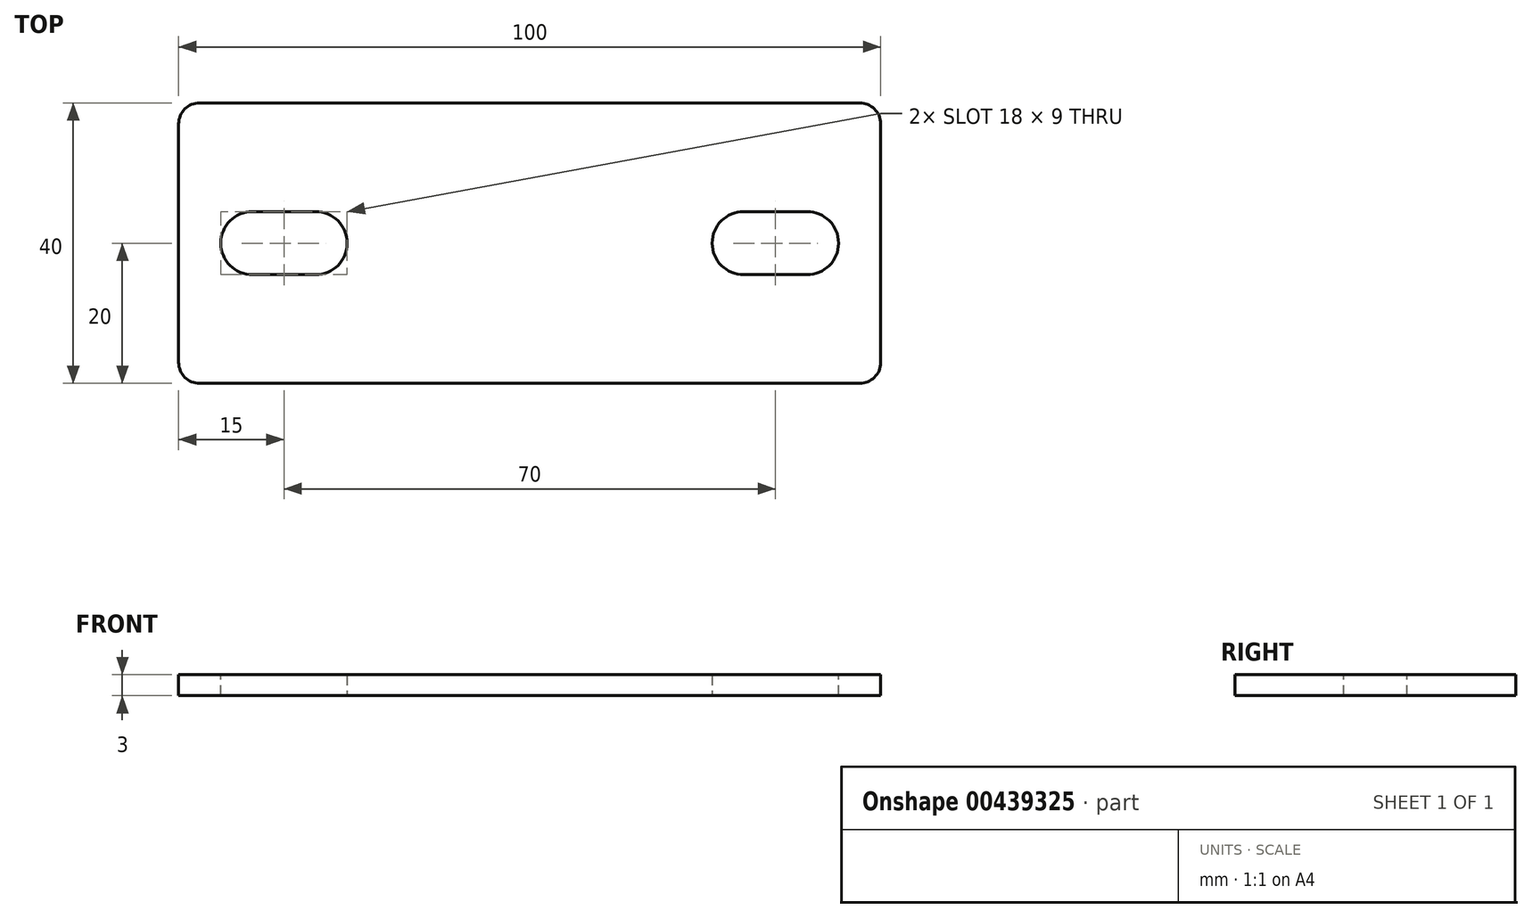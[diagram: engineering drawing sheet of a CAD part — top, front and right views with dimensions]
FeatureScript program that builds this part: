
annotation { "Feature Type Name" : "Feature", "Feature Type Description" : "" }
export const myFeature = defineFeature(function(context is Context, id is Id, definition is map)
    precondition{}
    {
        {
            var Q0;
            Q0=qCreatedBy(makeId("Top.planeOp"),FACE);
            var sketch = newSketch(context, id + "F0", { "sketchPlane" : qUnion([Q0])});
            skLineSegment(sketch, "E0.bottom", {"start": v(50, 20) * mm, "end": v(-50, 20) * mm});
            skLineSegment(sketch, "E0.top", {"start": v(50, -20) * mm, "end": v(-50, -20) * mm});
            skLineSegment(sketch, "E0.left", {"start": v(50, 20) * mm, "end": v(50, -20) * mm});
            skLineSegment(sketch, "E0.right", {"start": v(-50, 20) * mm, "end": v(-50, -20) * mm});
            skPoint(sketch, "E0.middle", {"position": v(0, 0) * mm});
            skSolve(sketch);
        }
        {
            var Q0;
            Q0=makeQuery(id+"F0.imprint","IMPRINT",FACE,{"disambiguationData":[TD([[makeQuery(id+"F0.imprint","IMPRINT",EDGE,{"derivedFrom":sQuery(id+"F0.wireOp",EDGE,"E0.bottom")}),1.0]])]});
            extrude(context, id + "F1", {"entities" : qUnion([Q0]), "depth" : 3 * mm});
        }
        {
            var Q0;
            Q0=makeQuery(id+"F1.opExtrude","SWEPT_EDGE",EDGE,{"disambiguationData":[OSD([sQuery(id+"F0.wireOp",EDGE,"E0.top"),sQuery(id+"F0.wireOp",EDGE,"E0.left")])]});
            var Q1;
            Q1=makeQuery(id+"F1.opExtrude","SWEPT_EDGE",EDGE,{"disambiguationData":[OSD([sQuery(id+"F0.wireOp",EDGE,"E0.bottom"),sQuery(id+"F0.wireOp",EDGE,"E0.left")])]});
            var Q2;
            Q2=makeQuery(id+"F1.opExtrude","SWEPT_EDGE",EDGE,{"disambiguationData":[OSD([sQuery(id+"F0.wireOp",EDGE,"E0.top"),sQuery(id+"F0.wireOp",EDGE,"E0.right")])]});
            var Q3;
            Q3=makeQuery(id+"F1.opExtrude","SWEPT_EDGE",EDGE,{"disambiguationData":[OSD([sQuery(id+"F0.wireOp",EDGE,"E0.bottom"),sQuery(id+"F0.wireOp",EDGE,"E0.right")])]});
            fillet(context, id + "F2", {"entities" : qUnion([Q0, Q1, Q2, Q3]), "radius" : 3 * mm, "tangentPropagation" : true, "allowEdgeOverflow" : false});
        }
        {
            var Q0;
            Q0=makeQuery(id+"F1.opExtrude","CAP_FACE",FACE,{"disambiguationData":[OSD([sQuery(id+"F0.wireOp",EDGE,"E0.bottom"),sQuery(id+"F0.wireOp",EDGE,"E0.top"),sQuery(id+"F0.wireOp",EDGE,"E0.left"),sQuery(id+"F0.wireOp",EDGE,"E0.right")])],"isStart":false});
            var sketch = newSketch(context, id + "F3", { "sketchPlane" : qUnion([Q0])});
            skLineSegment(sketch, "E1.bottom", {"start": v(-26, -4.5) * mm, "end": v(-44, -4.5) * mm});
            skLineSegment(sketch, "E1.top", {"start": v(-26, 4.5) * mm, "end": v(-44, 4.5) * mm});
            skLineSegment(sketch, "E1.left", {"start": v(-26, -4.5) * mm, "end": v(-26, 4.5) * mm});
            skLineSegment(sketch, "E1.right", {"start": v(-44, -4.5) * mm, "end": v(-44, 4.5) * mm});
            skPoint(sketch, "E1.middle", {"position": v(-35, 0) * mm});
            skPoint(sketch, "E1.middle.positionSnap0", {"position": v(-50, 0) * mm});
            skPoint(sketch, "E1.centerSnap0", {"position": v(-50, 0) * mm});
            skPoint(sketch, "E2.MirrorP", {"position": v(50, 0) * mm});
            skPoint(sketch, "E3.MirrorP", {"position": v(35, 0) * mm});
            skLineSegment(sketch, "E4.MirrorCS", {"start": v(44, -4.5) * mm, "end": v(44, 4.5) * mm});
            skLineSegment(sketch, "E5.MirrorCS", {"start": v(26, -4.5) * mm, "end": v(26, 4.5) * mm});
            skLineSegment(sketch, "E6.MirrorCS", {"start": v(26, -4.5) * mm, "end": v(44, -4.5) * mm});
            skLineSegment(sketch, "E7.MirrorCS", {"start": v(26, 4.5) * mm, "end": v(44, 4.5) * mm});
            skSolve(sketch);
        }
        {
            var Q0;
            Q0=makeQuery(id+"F3.imprint","IMPRINT",FACE,{"disambiguationData":[TD([[makeQuery(id+"F3.imprint","IMPRINT",EDGE,{"derivedFrom":sQuery(id+"F3.wireOp",EDGE,"E1.bottom")}),-1.0]])]});
            var Q1;
            Q1=makeQuery(id+"F3.imprint","IMPRINT",FACE,{"disambiguationData":[TD([[makeQuery(id+"F3.imprint","IMPRINT",EDGE,{"derivedFrom":sQuery(id+"F3.wireOp",EDGE,"E4.MirrorCS")}),1.0]])]});
            extrude(context, id + "F4", {"entities" : qUnion([Q0, Q1]), "operationType" : NewBodyOperationType.REMOVE, "oppositeDirection" : true, "depth" : 25 * mm});
        }
        {
            var Q0;
            Q0=makeQuery(id+"F4.boolean.opBoolean","COPY",EDGE,{"derivedFrom":makeQuery(id+"F4.opExtrude","SWEPT_EDGE",EDGE,{"disambiguationData":[OSD([sQuery(id+"F3.wireOp",EDGE,"E1.top"),sQuery(id+"F3.wireOp",EDGE,"E1.right")])]})});
            var Q1;
            Q1=makeQuery(id+"F4.boolean.opBoolean","COPY",EDGE,{"derivedFrom":makeQuery(id+"F4.opExtrude","SWEPT_EDGE",EDGE,{"disambiguationData":[OSD([sQuery(id+"F3.wireOp",EDGE,"E1.top"),sQuery(id+"F3.wireOp",EDGE,"E1.left")])]})});
            var Q2;
            Q2=makeQuery(id+"F4.boolean.opBoolean","COPY",EDGE,{"derivedFrom":makeQuery(id+"F4.opExtrude","SWEPT_EDGE",EDGE,{"disambiguationData":[OSD([sQuery(id+"F3.wireOp",EDGE,"E1.bottom"),sQuery(id+"F3.wireOp",EDGE,"E1.left")])]})});
            var Q3;
            Q3=makeQuery(id+"F4.boolean.opBoolean","COPY",EDGE,{"derivedFrom":makeQuery(id+"F4.opExtrude","SWEPT_EDGE",EDGE,{"disambiguationData":[OSD([sQuery(id+"F3.wireOp",EDGE,"E1.bottom"),sQuery(id+"F3.wireOp",EDGE,"E1.right")])]})});
            fillet(context, id + "F5", {"entities" : qUnion([Q0, Q1, Q2, Q3]), "radius" : 4.5 * mm, "tangentPropagation" : true, "allowEdgeOverflow" : false});
        }
        {
            var Q0;
            Q0=makeQuery(id+"F4.boolean.opBoolean","COPY",EDGE,{"derivedFrom":makeQuery(id+"F4.opExtrude","SWEPT_EDGE",EDGE,{"disambiguationData":[OSD([sQuery(id+"F3.wireOp",EDGE,"E5.MirrorCS"),sQuery(id+"F3.wireOp",EDGE,"E7.MirrorCS")])]})});
            var Q1;
            Q1=makeQuery(id+"F4.boolean.opBoolean","COPY",EDGE,{"derivedFrom":makeQuery(id+"F4.opExtrude","SWEPT_EDGE",EDGE,{"disambiguationData":[OSD([sQuery(id+"F3.wireOp",EDGE,"E4.MirrorCS"),sQuery(id+"F3.wireOp",EDGE,"E7.MirrorCS")])]})});
            var Q2;
            Q2=makeQuery(id+"F4.boolean.opBoolean","COPY",EDGE,{"derivedFrom":makeQuery(id+"F4.opExtrude","SWEPT_EDGE",EDGE,{"disambiguationData":[OSD([sQuery(id+"F3.wireOp",EDGE,"E4.MirrorCS"),sQuery(id+"F3.wireOp",EDGE,"E6.MirrorCS")])]})});
            var Q3;
            Q3=makeQuery(id+"F4.boolean.opBoolean","COPY",EDGE,{"derivedFrom":makeQuery(id+"F4.opExtrude","SWEPT_EDGE",EDGE,{"disambiguationData":[OSD([sQuery(id+"F3.wireOp",EDGE,"E5.MirrorCS"),sQuery(id+"F3.wireOp",EDGE,"E6.MirrorCS")])]})});
            fillet(context, id + "F6", {"entities" : qUnion([Q0, Q1, Q2, Q3]), "radius" : 4.5 * mm, "tangentPropagation" : true, "allowEdgeOverflow" : false});
        }
    });
